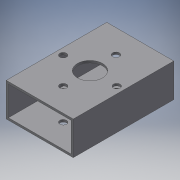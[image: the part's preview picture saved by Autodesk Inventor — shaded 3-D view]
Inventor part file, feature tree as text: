
AUTODESK INVENTOR PART (.ipt)
format: ipt  version: 2018 (Build 220112000, 112)  size: 140,288 bytes
history: native  units: in
note: dims shown in document units (in); Inventor stores cm internally (conversion verified against a paired STEP export)
features: extrude x3, sketch x3
ambient origin geometry x8: Origin, YZ Plane, XZ Plane, XY Plane, X Axis, Y Axis, Z Axis, Center Point
bodies: Solid1 (feature_tree)
feature tree (6):
  extrude  "Extrusion1"  Depth=1.0in
  extrude  "Extrusion2"  Depth=0.065in
  extrude  "Extrusion3"  Depth=0.065in
  sketch  "Sketch1"  dims[d0=0.065in d1=1.0in]
  sketch  "Sketch2"  dims[d2=2.0in d3=0.065in]
  sketch  "Sketch3"  dims[d4=0.065in d5=0.065in d6=3.0in d7=0.0in d8=0.75in d9=1.0in d10=1.5in d11=3.0in d12=0.0in d13=0.8in d14=0.0in d15=0.8in d16=0.0in d17=0.8in d18=0.2031in d19=0.2031in d20=0.0in d21=0.8in d22=0.2031in d23=0.2031in d24=3.0in d25=0.0in]
